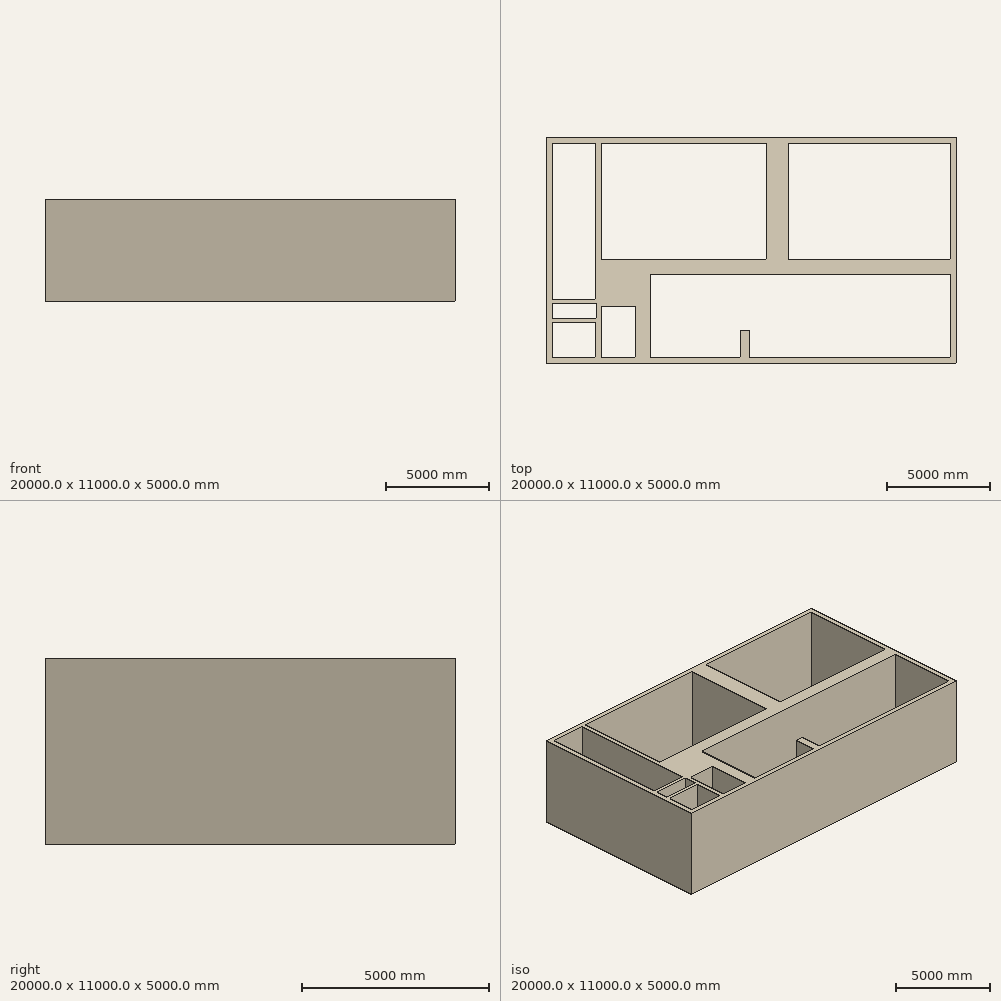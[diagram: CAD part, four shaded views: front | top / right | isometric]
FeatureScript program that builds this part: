
annotation { "Feature Type Name" : "Feature", "Feature Type Description" : "" }
export const myFeature = defineFeature(function(context is Context, id is Id, definition is map)
    precondition{}
    {
        {
            var Q0;
            Q0=qCreatedBy(makeId("Top.planeOp"),FACE);
            var sketch = newSketch(context, id + "F0", { "sketchPlane" : qUnion([Q0])});
            skLineSegment(sketch, "E0.bottom", {"start": v(0, 14000) * mm, "end": v(20000, 14000) * mm});
            skLineSegment(sketch, "E0.top", {"start": v(0, 3000) * mm, "end": v(20000, 3000) * mm});
            skLineSegment(sketch, "E0.left", {"start": v(0, 14000) * mm, "end": v(0, 3000) * mm});
            skLineSegment(sketch, "E0.right", {"start": v(20000, 14000) * mm, "end": v(20000, 3000) * mm});
            skLineSegment(sketch, "E1.bottom", {"start": v(2000, 3000) * mm, "end": v(12000, 3000) * mm});
            skLineSegment(sketch, "E1.top", {"start": v(2000, 0) * mm, "end": v(12000, 0) * mm});
            skLineSegment(sketch, "E1.left", {"start": v(2000, 3000) * mm, "end": v(2000, 0) * mm});
            skLineSegment(sketch, "E1.right", {"start": v(12000, 3000) * mm, "end": v(12000, 0) * mm});
            skLineSegment(sketch, "E2.bottom", {"start": v(19700, 13700) * mm, "end": v(11791.1, 13700) * mm});
            skLineSegment(sketch, "E2.top", {"start": v(19700, 8073.2) * mm, "end": v(11791.1, 8073.2) * mm});
            skLineSegment(sketch, "E2.left", {"start": v(19700, 13700) * mm, "end": v(19700, 8073.2) * mm});
            skLineSegment(sketch, "E2.right", {"start": v(11791.1, 13700) * mm, "end": v(11791.1, 8073.2) * mm});
            skLineSegment(sketch, "E3.bottom", {"start": v(2672.8, 13700) * mm, "end": v(10716.83, 13700) * mm});
            skLineSegment(sketch, "E3.top", {"start": v(2672.8, 8073.2) * mm, "end": v(10716.83, 8073.2) * mm});
            skLineSegment(sketch, "E3.left", {"start": v(2672.8, 13700) * mm, "end": v(2672.8, 8073.2) * mm});
            skLineSegment(sketch, "E3.right", {"start": v(10716.83, 13700) * mm, "end": v(10716.83, 8073.2) * mm});
            skLineSegment(sketch, "E4.bottom", {"start": v(5066.7, 7313.45) * mm, "end": v(19700, 7313.45) * mm});
            skLineSegment(sketch, "E4.top", {"start": v(5066.7, 3300) * mm, "end": v(19700, 3300) * mm});
            skLineSegment(sketch, "E4.left", {"start": v(5066.7, 7313.45) * mm, "end": v(5066.7, 3300) * mm});
            skLineSegment(sketch, "E4.right", {"start": v(19700, 7313.45) * mm, "end": v(19700, 3300) * mm});
            skLineSegment(sketch, "E5.bottom", {"start": v(300, 13700) * mm, "end": v(2409.65, 13700) * mm});
            skLineSegment(sketch, "E5.top", {"start": v(300, 6109.82) * mm, "end": v(2409.65, 6109.82) * mm});
            skLineSegment(sketch, "E5.left", {"start": v(300, 13700) * mm, "end": v(300, 6109.82) * mm});
            skLineSegment(sketch, "E5.right", {"start": v(2409.65, 13700) * mm, "end": v(2409.65, 6109.82) * mm});
            skLineSegment(sketch, "E6.bottom", {"start": v(300, 5918.04) * mm, "end": v(2433.63, 5918.04) * mm});
            skLineSegment(sketch, "E6.top", {"start": v(300, 5174.86) * mm, "end": v(2433.63, 5174.86) * mm});
            skLineSegment(sketch, "E6.left", {"start": v(300, 5918.04) * mm, "end": v(300, 5174.86) * mm});
            skLineSegment(sketch, "E6.right", {"start": v(2433.63, 5918.04) * mm, "end": v(2433.63, 5174.86) * mm});
            skLineSegment(sketch, "E7.bottom", {"start": v(300, 4983.08) * mm, "end": v(2397.67, 4983.08) * mm});
            skLineSegment(sketch, "E7.top", {"start": v(300, 3300) * mm, "end": v(2397.67, 3300) * mm});
            skLineSegment(sketch, "E7.left", {"start": v(300, 4983.08) * mm, "end": v(300, 3300) * mm});
            skLineSegment(sketch, "E7.right", {"start": v(2397.67, 4983.08) * mm, "end": v(2397.67, 3300) * mm});
            skLineSegment(sketch, "E8.bottom", {"start": v(2672.8, 5769.25) * mm, "end": v(4338.95, 5769.25) * mm});
            skLineSegment(sketch, "E8.top", {"start": v(2672.8, 3300) * mm, "end": v(4338.95, 3300) * mm});
            skLineSegment(sketch, "E8.left", {"start": v(2672.8, 5769.25) * mm, "end": v(2672.8, 3300) * mm});
            skLineSegment(sketch, "E8.right", {"start": v(4338.95, 5769.25) * mm, "end": v(4338.95, 3300) * mm});
            skLineSegment(sketch, "E9.bottom", {"start": v(9482.06, 3300) * mm, "end": v(9925.56, 3300) * mm});
            skLineSegment(sketch, "E9.top", {"start": v(9482.06, 4574.4) * mm, "end": v(9925.56, 4574.4) * mm});
            skLineSegment(sketch, "E9.left", {"start": v(9482.06, 3300) * mm, "end": v(9482.06, 4574.4) * mm});
            skLineSegment(sketch, "E9.right", {"start": v(9925.56, 3300) * mm, "end": v(9925.56, 4574.4) * mm});
            skLineSegment(sketch, "E10.bottom", {"start": v(11700, 300) * mm, "end": v(7918.18, 300) * mm});
            skLineSegment(sketch, "E10.top", {"start": v(11700, 2830.94) * mm, "end": v(7918.18, 2830.94) * mm});
            skLineSegment(sketch, "E10.left", {"start": v(11700, 300) * mm, "end": v(11700, 2830.94) * mm});
            skLineSegment(sketch, "E10.right", {"start": v(7918.18, 300) * mm, "end": v(7918.18, 2830.94) * mm});
            skLineSegment(sketch, "E11.bottom", {"start": v(7715.94, 2830.94) * mm, "end": v(5661.04, 2830.94) * mm});
            skLineSegment(sketch, "E11.top", {"start": v(7715.94, 300) * mm, "end": v(5661.04, 300) * mm});
            skLineSegment(sketch, "E11.left", {"start": v(7715.94, 2830.94) * mm, "end": v(7715.94, 300) * mm});
            skLineSegment(sketch, "E11.right", {"start": v(5661.04, 2830.94) * mm, "end": v(5661.04, 300) * mm});
            skLineSegment(sketch, "E12.bottom", {"start": v(2300, 2830.94) * mm, "end": v(4631, 2830.94) * mm});
            skLineSegment(sketch, "E12.top", {"start": v(2300, 303.1) * mm, "end": v(4631, 303.1) * mm});
            skLineSegment(sketch, "E12.left", {"start": v(2300, 2830.94) * mm, "end": v(2300, 303.1) * mm});
            skLineSegment(sketch, "E12.right", {"start": v(4631, 2830.94) * mm, "end": v(4631, 303.1) * mm});
            skSolve(sketch);
        }
        {
            var Q0;
            Q0=makeQuery(id+"F0.imprint","IMPRINT",FACE,{"disambiguationData":[TD([[makeQuery(id+"F0.imprint","IMPRINT",EDGE,{"derivedFrom":sQuery(id+"F0.wireOp",EDGE,"E0.bottom")}),-1.0]])]});
            var Q1;
            Q1=makeQuery(id+"F0.imprint","IMPRINT",FACE,{"disambiguationData":[TD([[makeQuery(id+"F0.imprint","IMPRINT",EDGE,{"derivedFrom":sQuery(id+"F0.wireOp",EDGE,"E9.top")}),-1.0]])]});
            extrude(context, id + "F1", {"entities" : qUnion([Q0, Q1]), "flatOperationType" : FlatOperationType.REMOVE, "depth" : 5000 * mm, "offsetDistance" : 25 * mm, "domain" : OperationDomain.MODEL});
        }
    });
